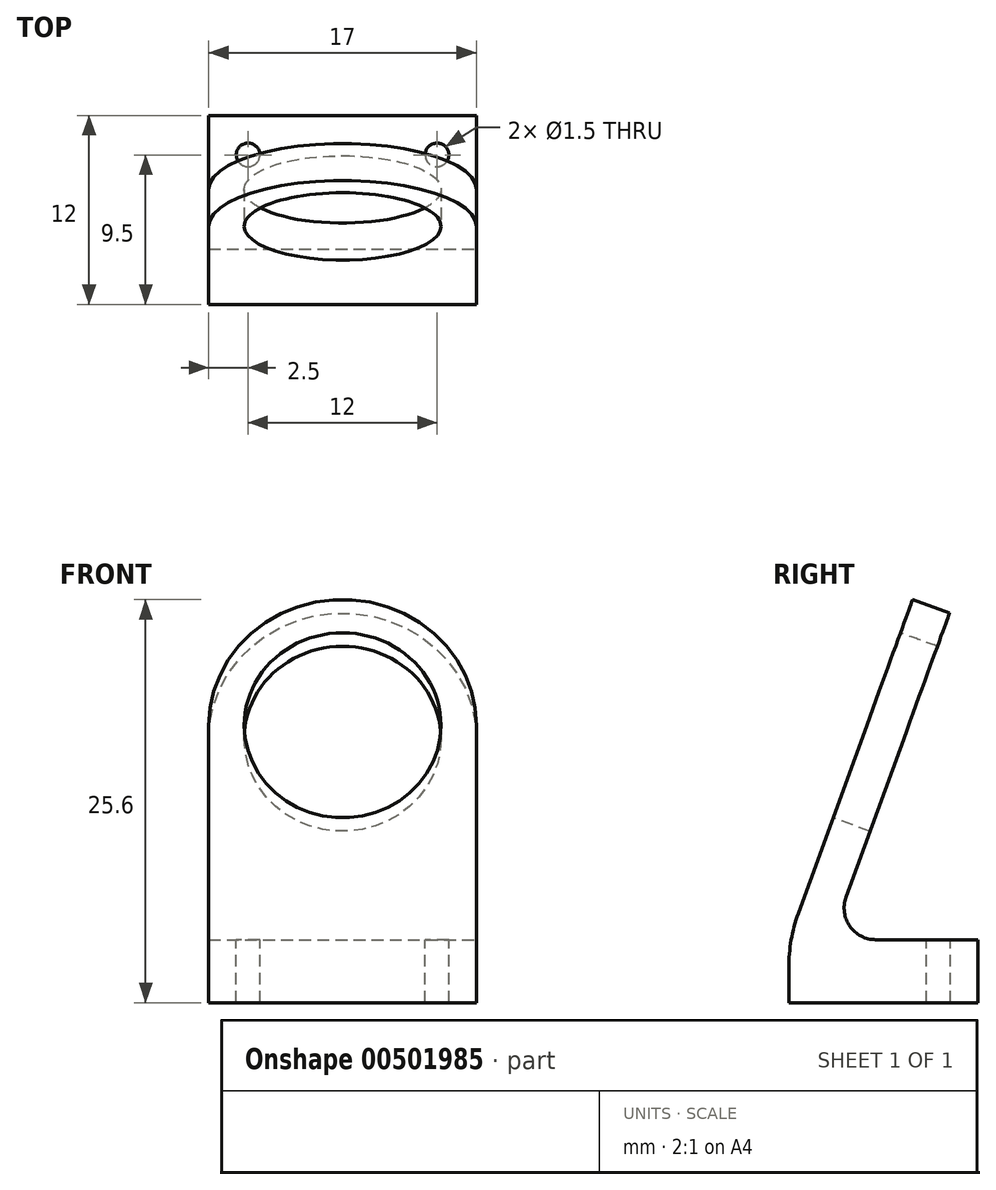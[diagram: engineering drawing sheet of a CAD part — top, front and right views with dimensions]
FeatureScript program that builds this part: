
annotation { "Feature Type Name" : "Feature", "Feature Type Description" : "" }
export const myFeature = defineFeature(function(context is Context, id is Id, definition is map)
    precondition{}
    {
        {
            var Q0;
            Q0=qCreatedBy(makeId("Top.planeOp"),FACE);
            var sketch = newSketch(context, id + "F0", { "sketchPlane" : qUnion([Q0])});
            skLineSegment(sketch, "E0.bottom", {"start": v(-8.5, 0) * mm, "end": v(8.5, 0) * mm});
            skLineSegment(sketch, "E0.top", {"start": v(-8.5, -12) * mm, "end": v(8.5, -12) * mm});
            skLineSegment(sketch, "E0.left", {"start": v(-8.5, 0) * mm, "end": v(-8.5, -12) * mm});
            skLineSegment(sketch, "E0.right", {"start": v(8.5, 0) * mm, "end": v(8.5, -12) * mm});
            skPoint(sketch, "E1", {"position": v(0, 0) * mm});
            skSolve(sketch);
        }
        {
            var Q0;
            Q0=makeQuery(id+"F0.imprint","IMPRINT",FACE,{"disambiguationData":[TD([[makeQuery(id+"F0.imprint","IMPRINT",EDGE,{"derivedFrom":sQuery(id+"F0.wireOp",EDGE,"E0.bottom")}),-1.0]])]});
            extrude(context, id + "F1", {"entities" : qUnion([Q0]), "depth" : 4 * mm});
        }
        {
            var Q0;
            Q0=makeQuery(id+"F1.opExtrude","CAP_FACE",FACE,{"disambiguationData":[OSD([sQuery(id+"F0.wireOp",EDGE,"E0.bottom"),sQuery(id+"F0.wireOp",EDGE,"E0.top"),sQuery(id+"F0.wireOp",EDGE,"E0.left"),sQuery(id+"F0.wireOp",EDGE,"E0.right")])],"isStart":false});
            var sketch = newSketch(context, id + "F2", { "sketchPlane" : qUnion([Q0])});
            skCircle(sketch, "E2", {"center": v(-6, -2.5) * mm, "radius": 0.75 * mm});
            skCircle(sketch, "E3", {"center": v(6, -2.5) * mm, "radius": 0.75 * mm});
            skLineSegment(sketch, "E4", {"start": v(0, 4.14) * mm, "end": v(0, -14.52) * mm});
            skSolve(sketch);
        }
        {
            var Q0;
            Q0 = qSketchRegion(id + "F2", true);
            extrude(context, id + "F3", {"entities" : qUnion([Q0]), "operationType" : NewBodyOperationType.REMOVE, "oppositeDirection" : true, "depth" : 25 * mm});
        }
        {
            var Q0;
            Q0=makeQuery(id+"F1.opExtrude","CAP_EDGE",EDGE,{"disambiguationData":[OSD([sQuery(id+"F0.wireOp",EDGE,"E0.top")])],"isStart":false});
            cPlane(context, id + "F4", {"entities" : qUnion([Q0]), "cplaneType" : CPlaneType.LINE_ANGLE, "offset" : 25 * mm, "angle" : 20 * degree, "oppositeDirection" : true, "width" : 150 * mm, "height" : 150 * mm});
        }
        {
            var Q0;
            Q0=qCreatedBy(id+"F4.planeOp",FACE);
            var sketch = newSketch(context, id + "F5", { "sketchPlane" : qUnion([Q0])});
            skLineSegment(sketch, "E5", {"start": v(0, -0.35) * mm, "end": v(0, 28.64) * mm, "construction": true});
            skCircle(sketch, "E6", {"center": v(0, 14.15) * mm, "radius": 6.25 * mm});
            skPoint(sketch, "E7", {"position": v(0, 7.9) * mm});
            skLineSegment(sketch, "E8.bottom", {"start": v(8.5, -0.35) * mm, "end": v(-8.5, -0.35) * mm});
            skLineSegment(sketch, "E8.left", {"start": v(8.5, -0.35) * mm, "end": v(8.5, 14.15) * mm});
            skLineSegment(sketch, "E8.right", {"start": v(-8.5, -0.35) * mm, "end": v(-8.5, 14.15) * mm});
            skArc(sketch, "E9", {"start": v(8.5, 14.15) * mm, "mid": v(0, 22.65) * mm, "end": v(-8.5, 14.15) * mm});
            skSolve(sketch);
        }
        {
            var Q0;
            Q0=makeQuery(id+"F5.imprint","IMPRINT",FACE,{"disambiguationData":[TD([[makeQuery(id+"F5.imprint","IMPRINT",EDGE,{"derivedFrom":sQuery(id+"F5.wireOp",EDGE,"E6")}),-1.0]])]});
            extrude(context, id + "F6", {"entities" : qUnion([Q0]), "operationType" : NewBodyOperationType.ADD, "depth" : 2.5 * mm});
        }
        {
            var Q0;
            Q0=makeQuery(id+"F6.boolean.opBoolean","INTERSECT",EDGE,{"derivedFrom":[makeQuery(id+"F1.opExtrude","CAP_FACE",FACE,{"disambiguationData":[OSD([sQuery(id+"F0.wireOp",EDGE,"E0.bottom"),sQuery(id+"F0.wireOp",EDGE,"E0.top"),sQuery(id+"F0.wireOp",EDGE,"E0.left"),sQuery(id+"F0.wireOp",EDGE,"E0.right")])],"isStart":false}),makeQuery(id+"F6.opExtrude","CAP_FACE",FACE,{"disambiguationData":[OSD([sQuery(id+"F5.wireOp",EDGE,"E6"),sQuery(id+"F5.wireOp",EDGE,"E8.bottom"),sQuery(id+"F5.wireOp",EDGE,"E8.left"),sQuery(id+"F5.wireOp",EDGE,"E8.right"),sQuery(id+"F5.wireOp",EDGE,"E9")])],"isStart":false})]});
            fillet(context, id + "F7", {"entities" : qUnion([Q0]), "radius" : 2 * mm, "tangentPropagation" : true, "allowEdgeOverflow" : false});
        }
        {
            var Q0;
            Q0=makeQuery(id+"F6.boolean.opBoolean","MERGE",EDGE,{"derivedFrom":[makeQuery(id+"F1.opExtrude","CAP_EDGE",EDGE,{"disambiguationData":[OSD([sQuery(id+"F0.wireOp",EDGE,"E0.top")])],"isStart":false}),makeQuery(id+"F6.opExtrude","CAP_EDGE",EDGE,{"disambiguationData":[OSD([sQuery(id+"F5.wireOp",EDGE,"E8.bottom")])],"isStart":true})]});
            fillet(context, id + "F8", {"entities" : qUnion([Q0]), "radius" : 10 * mm, "tangentPropagation" : true, "allowEdgeOverflow" : false});
        }
    });
